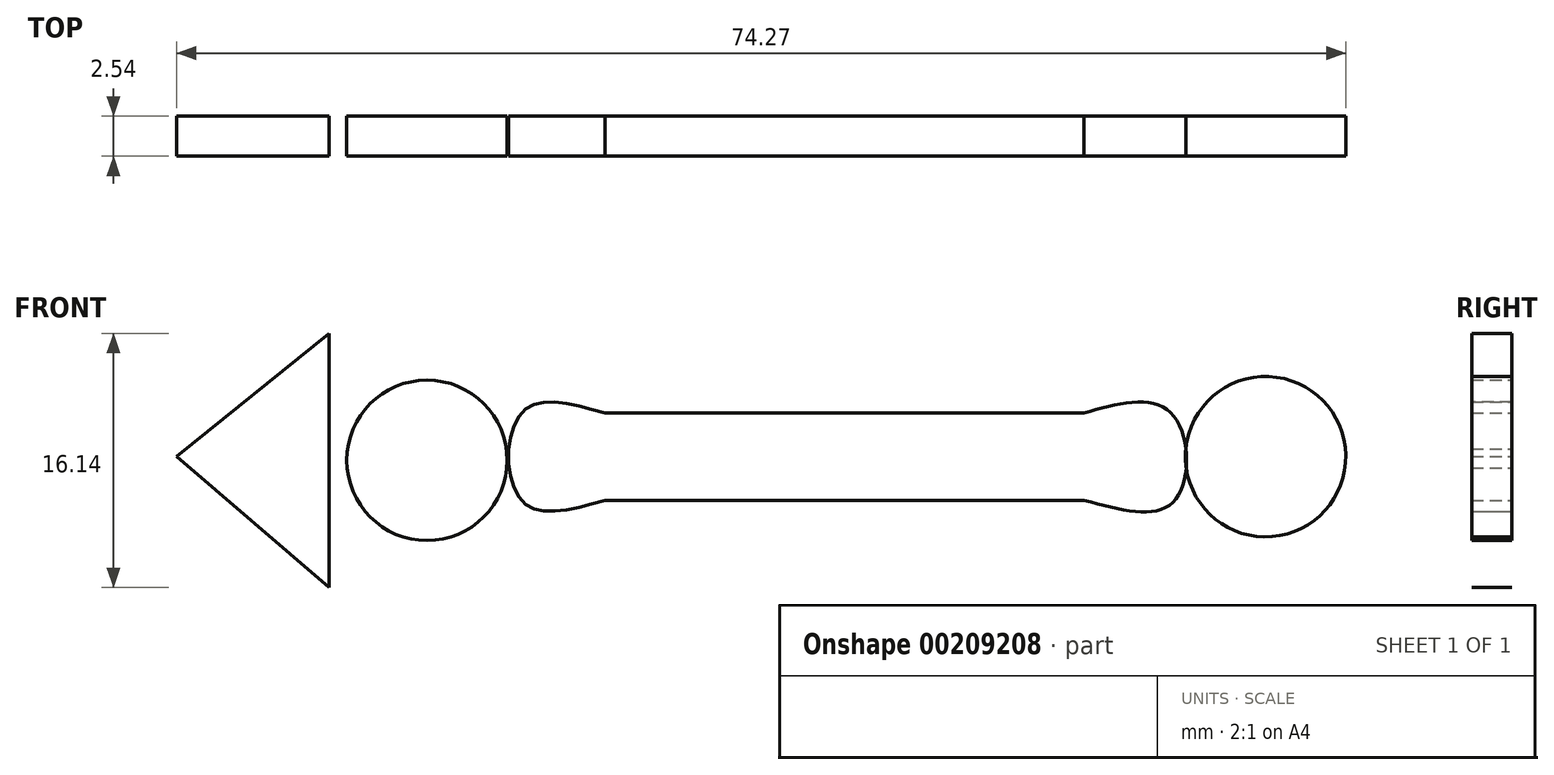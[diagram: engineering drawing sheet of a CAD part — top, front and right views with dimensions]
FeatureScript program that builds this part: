
annotation { "Feature Type Name" : "Feature", "Feature Type Description" : "" }
export const myFeature = defineFeature(function(context is Context, id is Id, definition is map)
    precondition{}
    {
        {
            var Q0;
            Q0=qCreatedBy(makeId("Front.planeOp"),FACE);
            var sketch = newSketch(context, id + "F0", { "sketchPlane" : qUnion([Q0])});
            skLineSegment(sketch, "E0.bottom", {"start": v(15.22, 2.77) * mm, "end": v(-15.22, 2.77) * mm});
            skLineSegment(sketch, "E0.top", {"start": v(15.22, -2.77) * mm, "end": v(-15.22, -2.77) * mm});
            skLineSegment(sketch, "E0.left", {"start": v(15.22, 2.77) * mm, "end": v(15.22, -2.77) * mm});
            skLineSegment(sketch, "E0.right", {"start": v(-15.22, 2.77) * mm, "end": v(-15.22, -2.77) * mm});
            skPoint(sketch, "E0.middle", {"position": v(0, 0) * mm});
            skFitSpline(sketch, "E1", {"points": [v(-15.22, 2.77) * mm, v(-20.52, 2.77) * mm, v(-20.52, -2.77) * mm, v(-15.22, -2.77) * mm], "startDerivative": vector(-19.38, 5.64) * mm, "endDerivative": vector(19.38, 5.64) * mm});
            skFitSpline(sketch, "E2", {"points": [v(15.22, 2.77) * mm, v(20.75, 2.77) * mm, v(20.98, -2.77) * mm, v(15.22, -2.77) * mm], "startDerivative": vector(18.37, 5.57) * mm, "endDerivative": vector(-21.15, 5.79) * mm});
            skCircle(sketch, "E3", {"center": v(26.75, 0) * mm, "radius": 5.1 * mm});
            skCircle(sketch, "E4", {"center": v(-26.52, -0.23) * mm, "radius": 5.1 * mm});
            skSolve(sketch);
        }
        {
            var Q0;
            Q0=makeQuery(id+"F0.imprint","IMPRINT",FACE,{"disambiguationData":[TD([[makeQuery(id+"F0.imprint","IMPRINT",EDGE,{"derivedFrom":sQuery(id+"F0.wireOp",EDGE,"E4")}),1.0]])]});
            var Q1;
            Q1=makeQuery(id+"F0.imprint","IMPRINT",FACE,{"disambiguationData":[TD([[makeQuery(id+"F0.imprint","IMPRINT",EDGE,{"derivedFrom":sQuery(id+"F0.wireOp",EDGE,"E0.right")}),-1.0]])]});
            var Q2;
            Q2=makeQuery(id+"F0.imprint","IMPRINT",FACE,{"disambiguationData":[TD([[makeQuery(id+"F0.imprint","IMPRINT",EDGE,{"derivedFrom":sQuery(id+"F0.wireOp",EDGE,"E0.bottom")}),1.0]])]});
            var Q3;
            {var subQ0=sQuery(id+"F0.wireOp",EDGE,"E0.left");Q3=makeQuery(id+"F0.imprint","IMPRINT",FACE,{"disambiguationData":[TD([[makeQuery(id+"F0.imprint","IMPRINT",EDGE,{"derivedFrom":subQ0}),1.0]])]});}
            var Q4;
            {var subQ0=sQuery(id+"F0.wireOp",EDGE,"E3");var subQ1=sQuery(id+"F0.wireOp",EDGE,"E2");var subQ2=makeQuery(id+"F0.imprint","INTERSECT",VERTEX,{"disambiguationData":[OD(0.0)],"derivedFrom":[subQ1,subQ0]});Q4=makeQuery(id+"F0.imprint","IMPRINT",FACE,{"disambiguationData":[TD([[makeQuery(id+"F0.imprint","IMPRINT",EDGE,{"disambiguationData":[TD([[subQ2,-1.0]])],"derivedFrom":subQ1}),1.0]])]});}
            extrude(context, id + "F1", {"entities" : qUnion([Q0, Q1, Q2, Q3, Q4]), "depth" : 2.54 * mm});
        }
        {
            var Q0;
            Q0=qCreatedBy(makeId("Front.planeOp"),FACE);
            var sketch = newSketch(context, id + "F2", { "sketchPlane" : qUnion([Q0])});
            skLineSegment(sketch, "E5", {"start": v(-32.74, 0) * mm, "end": v(-32.74, 7.84) * mm});
            skLineSegment(sketch, "E6", {"start": v(-32.74, 7.84) * mm, "end": v(-42.43, 0) * mm});
            skLineSegment(sketch, "E7", {"start": v(-42.43, 0) * mm, "end": v(-32.74, -8.3) * mm});
            skLineSegment(sketch, "E8", {"start": v(-32.74, -8.3) * mm, "end": v(-32.74, 0) * mm});
            skSolve(sketch);
        }
        {
            var Q0;
            Q0 = qSketchRegion(id + "F2", true);
            extrude(context, id + "F3", {"entities" : qUnion([Q0]), "depth" : 2.54 * mm});
        }
    });
